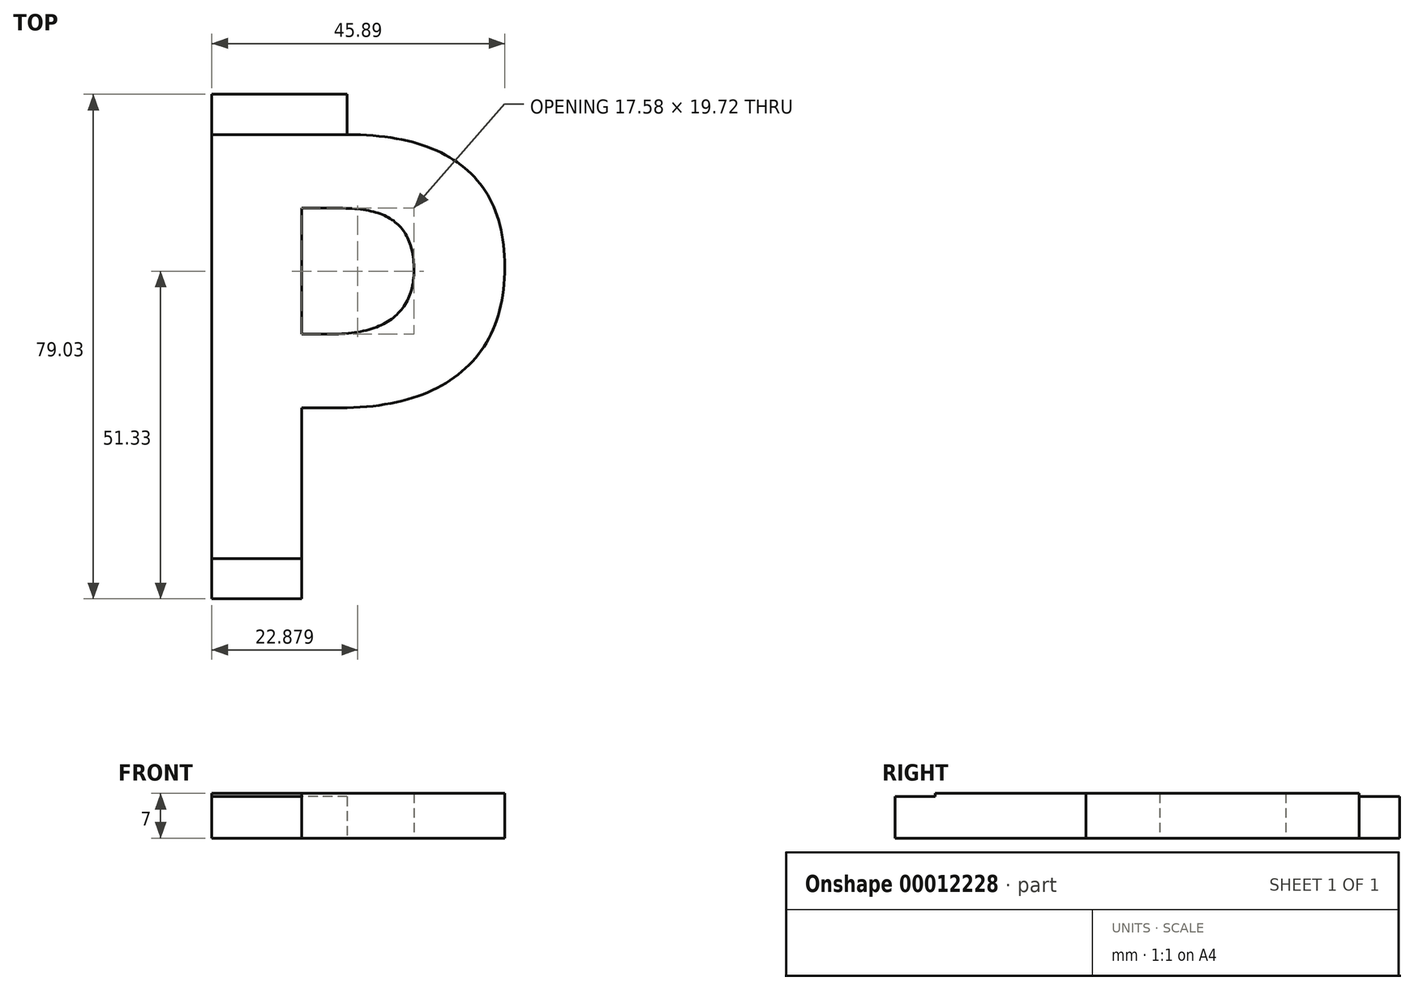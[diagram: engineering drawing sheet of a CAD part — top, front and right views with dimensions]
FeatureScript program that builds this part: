
annotation { "Feature Type Name" : "Feature", "Feature Type Description" : "" }
export const myFeature = defineFeature(function(context is Context, id is Id, definition is map)
    precondition{}
    {
        {
            var Q0;
            Q0=qCreatedBy(makeId("Top.planeOp"),FACE);
            var sketch = newSketch(context, id + "F0", { "sketchPlane" : qUnion([Q0])});
            skText(sketch, "E0", { "text": "P", "fontName": "OpenSans-Bold.ttf"});
            const initialGuessF0  = {"E0": [-0.05425, 0, 1, 0, 0.067]};
            skSetInitialGuess(sketch, initialGuessF0);
            skSolve(sketch);
        }
        {
            var Q0;
            Q0=makeQuery(id+"F0.imprint","IMPRINT",FACE,{"disambiguationData":[TD([[makeQuery(id+"F0.imprint","IMPRINT",EDGE,{"derivedFrom":sQuery(id+"F0.wireOp",EDGE,"E0.sketch_text.stroke-0")}),-1.0]])]});
            extrude(context, id + "F1", {"entities" : qUnion([Q0]), "depth" : 7 * mm});
        }
        {
            var Q0;
            Q0=makeQuery(id+"F1.opExtrude","SWEPT_FACE",FACE,{"disambiguationData":[OSD([sQuery(id+"F0.wireOp",EDGE,"E0.sketch_text.stroke-11")])]});
            var sketch = newSketch(context, id + "F2", { "sketchPlane" : qUnion([Q0])});
            skLineSegment(sketch, "E1.0.0", {"start": v(-45.89, 0) * mm, "end": v(-31.8, 0) * mm});
            skLineSegment(sketch, "E1.0.1", {"start": v(-31.8, 0) * mm, "end": v(-31.8, 7) * mm});
            skLineSegment(sketch, "E1.0.2", {"start": v(-31.8, 7) * mm, "end": v(-45.89, 7) * mm});
            skLineSegment(sketch, "E1.0.3", {"start": v(-45.89, 7) * mm, "end": v(-45.89, 0) * mm});
            skLineSegment(sketch, "E2.top", {"start": v(-45.89, 6.5) * mm, "end": v(-31.8, 6.5) * mm});
            skLineSegment(sketch, "E2.left", {"start": v(-45.89, 0) * mm, "end": v(-45.89, 6.5) * mm});
            skLineSegment(sketch, "E2.right", {"start": v(-31.8, 0) * mm, "end": v(-31.8, 6.5) * mm});
            skSolve(sketch);
        }
        {
            var Q0;
            Q0=makeQuery(id+"F2.imprint","IMPRINT",FACE,{"disambiguationData":[TD([[makeQuery(id+"F2.imprint","IMPRINT",EDGE,{"derivedFrom":sQuery(id+"F2.wireOp",EDGE,"E1.0.0")}),-1.0]])]});
            extrude(context, id + "F3", {"entities" : qUnion([Q0]), "operationType" : NewBodyOperationType.ADD, "depth" : 6.3 * mm});
        }
        {
            var Q0;
            Q0=makeQuery(id+"F1.opExtrude","SWEPT_FACE",FACE,{"disambiguationData":[OSD([sQuery(id+"F0.wireOp",EDGE,"E0.sketch_text.stroke-13")])]});
            var sketch = newSketch(context, id + "F4", { "sketchPlane" : qUnion([Q0])});
            skLineSegment(sketch, "E3.bottom", {"start": v(24.67, 0) * mm, "end": v(45.89, 0) * mm});
            skLineSegment(sketch, "E3.top", {"start": v(24.67, 6.5) * mm, "end": v(45.89, 6.5) * mm});
            skLineSegment(sketch, "E3.left", {"start": v(24.67, 0) * mm, "end": v(24.67, 6.5) * mm});
            skLineSegment(sketch, "E3.right", {"start": v(45.89, 0) * mm, "end": v(45.89, 6.5) * mm});
            skSolve(sketch);
        }
        {
            var Q0;
            Q0=makeQuery(id+"F4.imprint","IMPRINT",FACE,{"disambiguationData":[TD([[makeQuery(id+"F4.imprint","IMPRINT",EDGE,{"derivedFrom":sQuery(id+"F4.wireOp",EDGE,"E3.bottom")}),-1.0]])]});
            extrude(context, id + "F5", {"entities" : qUnion([Q0]), "operationType" : NewBodyOperationType.ADD, "depth" : 6.3 * mm});
        }
    });
